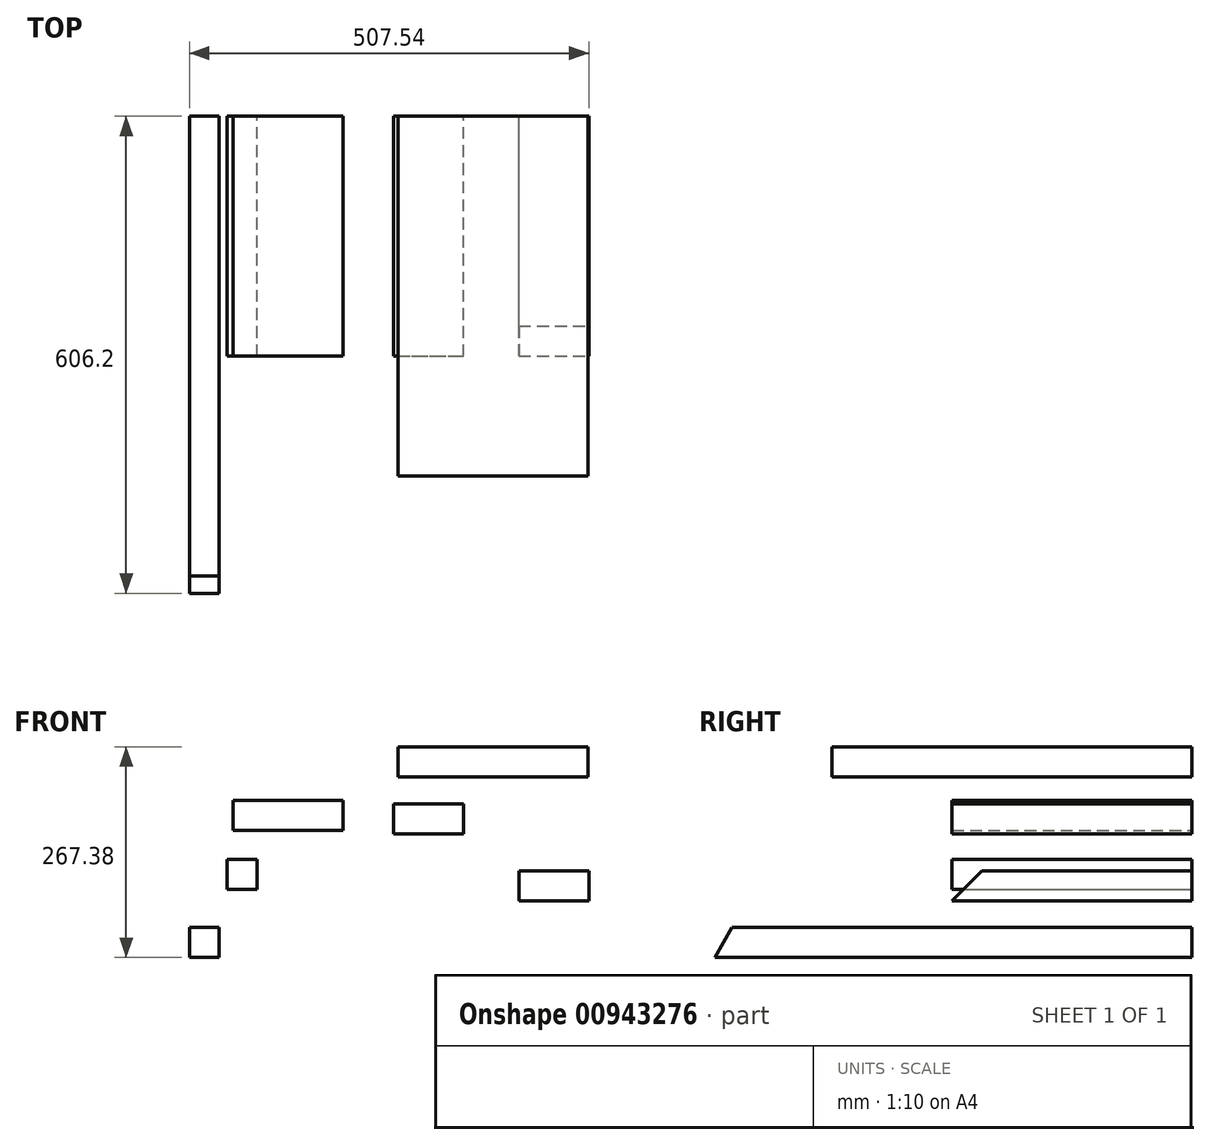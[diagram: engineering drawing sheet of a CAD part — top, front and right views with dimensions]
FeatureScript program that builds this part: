
annotation { "Feature Type Name" : "Feature", "Feature Type Description" : "" }
export const myFeature = defineFeature(function(context is Context, id is Id, definition is map)
    precondition{}
    {
        {
            var Q0;
            Q0=qCreatedBy(makeId("Front.planeOp"),FACE);
            var sketch = newSketch(context, id + "F0", { "sketchPlane" : qUnion([Q0])});
            skLineSegment(sketch, "E0.bottom", {"start": v(0, 0) * mm, "end": v(88.9, 0) * mm});
            skLineSegment(sketch, "E0.top", {"start": v(0, 38.1) * mm, "end": v(88.9, 38.1) * mm});
            skLineSegment(sketch, "E0.left", {"start": v(0, 0) * mm, "end": v(0, 38.1) * mm});
            skLineSegment(sketch, "E0.right", {"start": v(88.9, 0) * mm, "end": v(88.9, 38.1) * mm});
            skSolve(sketch);
        }
        {
            var Q0;
            Q0=makeQuery(id+"F0.imprint","IMPRINT",FACE,{"disambiguationData":[TD([[makeQuery(id+"F0.imprint","IMPRINT",EDGE,{"derivedFrom":sQuery(id+"F0.wireOp",EDGE,"E0.bottom")}),1.0]])]});
            extrude(context, id + "F1", {"entities" : qUnion([Q0]), "depth" : 304.8 * mm, "offsetDistance" : 25.4 * mm});
        }
        {
            var Q0;
            Q0=makeQuery(id+"F1.opExtrude","SWEPT_BODY",BODY,{"disambiguationData":[OSD([sQuery(id+"F0.wireOp",EDGE,"E0.bottom"),sQuery(id+"F0.wireOp",EDGE,"E0.top"),sQuery(id+"F0.wireOp",EDGE,"E0.left"),sQuery(id+"F0.wireOp",EDGE,"E0.right")])]});
            transform(context, id + "F2", {"entities" : qUnion([Q0]), "transformType" : TransformType.TRANSLATION_3D, "dx" : 127 * mm, "dy" : 0 * mm, "dz" : 0 * mm, "makeCopy" : true});
        }
        {
            var Q0;
            Q0=qCreatedBy(makeId("Front.planeOp"),FACE);
            var sketch = newSketch(context, id + "F3", { "sketchPlane" : qUnion([Q0])});
            skLineSegment(sketch, "E1.bottom", {"start": v(-204.08, 42.27) * mm, "end": v(-64.38, 42.27) * mm});
            skLineSegment(sketch, "E1.top", {"start": v(-204.08, 4.17) * mm, "end": v(-64.38, 4.17) * mm});
            skLineSegment(sketch, "E1.left", {"start": v(-204.08, 42.27) * mm, "end": v(-204.08, 4.17) * mm});
            skLineSegment(sketch, "E1.right", {"start": v(-64.38, 42.27) * mm, "end": v(-64.38, 4.17) * mm});
            skSolve(sketch);
        }
        {
            var Q0;
            Q0=makeQuery(id+"F3.imprint","IMPRINT",FACE,{"disambiguationData":[TD([[makeQuery(id+"F3.imprint","IMPRINT",EDGE,{"derivedFrom":sQuery(id+"F3.wireOp",EDGE,"E1.bottom")}),-1.0]])]});
            extrude(context, id + "F4", {"entities" : qUnion([Q0]), "depth" : 304.8 * mm, "offsetDistance" : 25.4 * mm});
        }
        {
            var Q0;
            Q0=makeQuery(id+"F2.opPattern","COPY",BODY,{"derivedFrom":makeQuery(id+"F1.opExtrude","SWEPT_BODY",BODY,{"disambiguationData":[OSD([sQuery(id+"F0.wireOp",EDGE,"E0.bottom"),sQuery(id+"F0.wireOp",EDGE,"E0.top"),sQuery(id+"F0.wireOp",EDGE,"E0.left"),sQuery(id+"F0.wireOp",EDGE,"E0.right")])]}),"instanceName":"1"});
            deleteBodies(context, id + "F5", {"entities" : qUnion([Q0])});
        }
        {
            var Q0;
            Q0=qCreatedBy(makeId("Front.planeOp"),FACE);
            var sketch = newSketch(context, id + "F6", { "sketchPlane" : qUnion([Q0])});
            skLineSegment(sketch, "E2.bottom", {"start": v(5.9, 110.4) * mm, "end": v(247.2, 110.4) * mm});
            skLineSegment(sketch, "E2.top", {"start": v(5.9, 72.3) * mm, "end": v(247.2, 72.3) * mm});
            skLineSegment(sketch, "E2.left", {"start": v(5.9, 110.4) * mm, "end": v(5.9, 72.3) * mm});
            skLineSegment(sketch, "E2.right", {"start": v(247.2, 110.4) * mm, "end": v(247.2, 72.3) * mm});
            skSolve(sketch);
        }
        {
            var Q0;
            Q0=makeQuery(id+"F6.imprint","IMPRINT",FACE,{"disambiguationData":[TD([[makeQuery(id+"F6.imprint","IMPRINT",EDGE,{"derivedFrom":sQuery(id+"F6.wireOp",EDGE,"E2.bottom")}),-1.0]])]});
            extrude(context, id + "F7", {"entities" : qUnion([Q0]), "depth" : 457.2 * mm, "offsetDistance" : 25.4 * mm});
        }
        {
            var Q0;
            Q0=qCreatedBy(makeId("Front.planeOp"),FACE);
            var sketch = newSketch(context, id + "F8", { "sketchPlane" : qUnion([Q0])});
            skLineSegment(sketch, "E3.bottom", {"start": v(-211.63, -32.62) * mm, "end": v(-173.53, -32.62) * mm});
            skLineSegment(sketch, "E3.top", {"start": v(-211.63, -70.72) * mm, "end": v(-173.53, -70.72) * mm});
            skLineSegment(sketch, "E3.left", {"start": v(-211.63, -32.62) * mm, "end": v(-211.63, -70.72) * mm});
            skLineSegment(sketch, "E3.right", {"start": v(-173.53, -32.62) * mm, "end": v(-173.53, -70.72) * mm});
            skSolve(sketch);
        }
        {
            var Q0;
            Q0=makeQuery(id+"F8.imprint","IMPRINT",FACE,{"disambiguationData":[TD([[makeQuery(id+"F8.imprint","IMPRINT",EDGE,{"derivedFrom":sQuery(id+"F8.wireOp",EDGE,"E3.bottom")}),-1.0]])]});
            extrude(context, id + "F9", {"entities" : qUnion([Q0]), "depth" : 304.8 * mm, "offsetDistance" : 25.4 * mm});
        }
        {
            var Q0;
            Q0=qCreatedBy(makeId("Front.planeOp"),FACE);
            var sketch = newSketch(context, id + "F10", { "sketchPlane" : qUnion([Q0])});
            skLineSegment(sketch, "E4.bottom", {"start": v(159.28, -47.07) * mm, "end": v(248.18, -47.07) * mm});
            skLineSegment(sketch, "E4.top", {"start": v(159.28, -85.17) * mm, "end": v(248.18, -85.17) * mm});
            skLineSegment(sketch, "E4.left", {"start": v(159.28, -47.07) * mm, "end": v(159.28, -85.17) * mm});
            skLineSegment(sketch, "E4.right", {"start": v(248.18, -47.07) * mm, "end": v(248.18, -85.17) * mm});
            skSolve(sketch);
        }
        {
            var Q0;
            Q0=makeQuery(id+"F10.imprint","IMPRINT",FACE,{"disambiguationData":[TD([[makeQuery(id+"F10.imprint","IMPRINT",EDGE,{"derivedFrom":sQuery(id+"F10.wireOp",EDGE,"E4.bottom")}),-1.0]])]});
            extrude(context, id + "F11", {"entities" : qUnion([Q0]), "depth" : 304.8 * mm, "offsetDistance" : 25.4 * mm});
        }
        {
            var Q0;
            Q0=makeQuery(id+"F11.opExtrude","CAP_EDGE",EDGE,{"disambiguationData":[OSD([sQuery(id+"F10.wireOp",EDGE,"E4.bottom")])],"isStart":false});
            chamfer(context, id + "F12", {"entities" : qUnion([Q0]), "width" : 38.1 * mm, "tangentPropagation" : true});
        }
        {
            var Q0;
            Q0=qCreatedBy(makeId("Front.planeOp"),FACE);
            var sketch = newSketch(context, id + "F13", { "sketchPlane" : qUnion([Q0])});
            skLineSegment(sketch, "E5.bottom", {"start": v(-259.36, -118.9) * mm, "end": v(-221.26, -118.9) * mm});
            skLineSegment(sketch, "E5.top", {"start": v(-259.36, -157) * mm, "end": v(-221.26, -157) * mm});
            skLineSegment(sketch, "E5.left", {"start": v(-259.36, -118.9) * mm, "end": v(-259.36, -157) * mm});
            skLineSegment(sketch, "E5.right", {"start": v(-221.26, -118.9) * mm, "end": v(-221.26, -157) * mm});
            skSolve(sketch);
        }
        {
            var Q0;
            Q0=makeQuery(id+"F13.imprint","IMPRINT",FACE,{"disambiguationData":[TD([[makeQuery(id+"F13.imprint","IMPRINT",EDGE,{"derivedFrom":sQuery(id+"F13.wireOp",EDGE,"E5.bottom")}),-1.0]])]});
            extrude(context, id + "F14", {"entities" : qUnion([Q0]), "depth" : 609.6 * mm, "offsetDistance" : 25.4 * mm});
        }
        {
            var Q0;
            Q0=makeQuery(id+"F14.opExtrude","CAP_EDGE",EDGE,{"disambiguationData":[OSD([sQuery(id+"F13.wireOp",EDGE,"E5.bottom")])],"isStart":false});
            chamfer(context, id + "F15", {"entities" : qUnion([Q0]), "chamferType" : ChamferType.OFFSET_ANGLE, "width" : 25.4 * mm, "oppositeDirection" : false, "angle" : 60 * degree, "tangentPropagation" : true});
        }
    });
